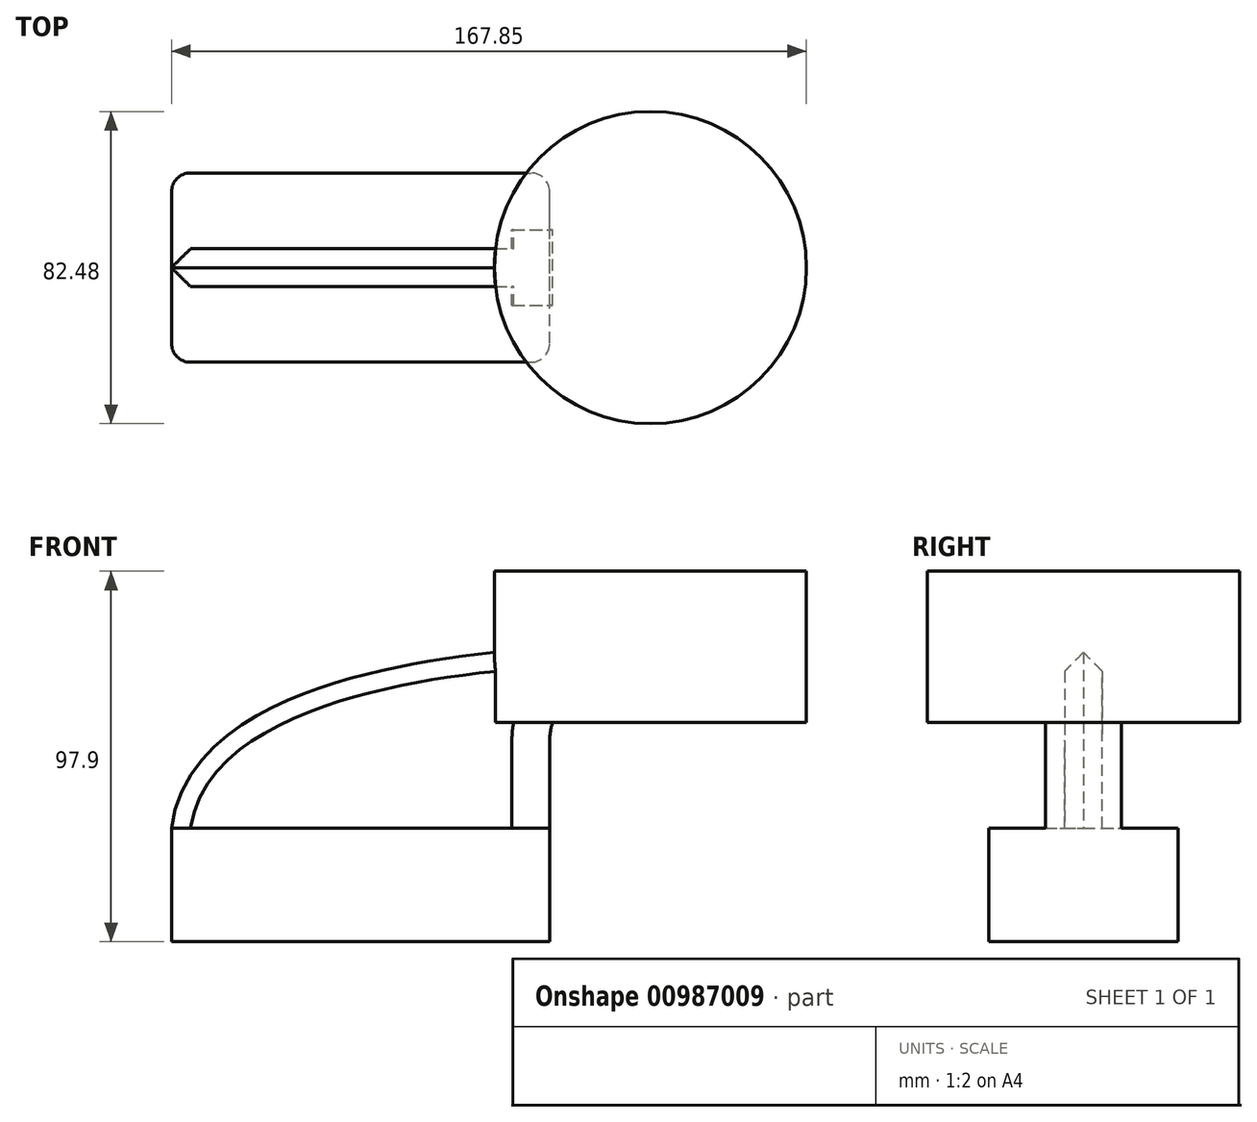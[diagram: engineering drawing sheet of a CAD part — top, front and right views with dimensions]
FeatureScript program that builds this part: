
annotation { "Feature Type Name" : "Feature", "Feature Type Description" : "" }
export const myFeature = defineFeature(function(context is Context, id is Id, definition is map)
    precondition{}
    {
        {
            var Q0;
            Q0=qCreatedBy(makeId("Front.planeOp"),FACE);
            var sketch = newSketch(context, id + "F0", { "sketchPlane" : qUnion([Q0])});
            skLineSegment(sketch, "E0.bottom", {"start": v(-50, 15) * mm, "end": v(50, 15) * mm});
            skLineSegment(sketch, "E0.top", {"start": v(-50, -15) * mm, "end": v(50, -15) * mm});
            skLineSegment(sketch, "E0.left", {"start": v(-50, 15) * mm, "end": v(-50, -15) * mm});
            skLineSegment(sketch, "E0.right", {"start": v(50, 15) * mm, "end": v(50, -15) * mm});
            skPoint(sketch, "E0.middle", {"position": v(0, 0) * mm});
            skLineSegment(sketch, "E1.bottom", {"start": v(76.6, 42.9) * mm, "end": v(117.85, 42.9) * mm});
            skLineSegment(sketch, "E1.top", {"start": v(76.6, 82.9) * mm, "end": v(117.85, 82.9) * mm});
            skLineSegment(sketch, "E1.left", {"start": v(76.6, 42.9) * mm, "end": v(76.6, 82.9) * mm});
            skLineSegment(sketch, "E1.right", {"start": v(117.85, 42.9) * mm, "end": v(117.85, 82.9) * mm});
            skPoint(sketch, "E1.middle", {"position": v(97.23, 62.9) * mm});
            skLineSegment(sketch, "E2", {"start": v(50, 15) * mm, "end": v(50, 38.22) * mm});
            skArc(sketch, "E3", {"start": v(50, 38.22) * mm, "mid": v(54.4, 48.82) * mm, "end": v(65, 53.22) * mm});
            skLineSegment(sketch, "E4", {"start": v(65, 53.22) * mm, "end": v(96.4, 53.22) * mm});
            skLineSegment(sketch, "E5.0", {"start": v(65, 63.22) * mm, "end": v(96.4, 63.22) * mm});
            skArc(sketch, "E5.1", {"start": v(40, 38.22) * mm, "mid": v(47.32, 55.9) * mm, "end": v(65, 63.22) * mm});
            skLineSegment(sketch, "E5.2", {"start": v(40, 15) * mm, "end": v(40, 38.22) * mm});
            skFitSpline(sketch, "E6", {"points": [v(-50, 15) * mm, v(65, 63.22) * mm], "startDerivative": vector(14.19, 117.72) * mm, "endDerivative": vector(125.03, 2.43) * mm});
            skSolve(sketch);
        }
        {
            var Q0;
            Q0=makeQuery(id+"F0.imprint","IMPRINT",FACE,{"disambiguationData":[TD([[makeQuery(id+"F0.imprint","IMPRINT",EDGE,{"derivedFrom":sQuery(id+"F0.wireOp",EDGE,"E0.top")}),1.0]])]});
            extrude(context, id + "F1", {"entities" : qUnion([Q0]), "endBound" : BoundingType.SYMMETRIC, "depth" : 50 * mm, "offsetDistance" : 25 * mm});
        }
        {
            var Q0;
            {var subQ1=sQuery(id+"F0.wireOp",EDGE,"E2");Q0=makeQuery(id+"F0.imprint","IMPRINT",FACE,{"disambiguationData":[TD([[makeQuery(id+"F0.imprint","IMPRINT",EDGE,{"derivedFrom":subQ1}),1.0]])]});}
            extrude(context, id + "F2", {"entities" : qUnion([Q0]), "operationType" : NewBodyOperationType.ADD, "endBound" : BoundingType.SYMMETRIC, "depth" : 20 * mm, "offsetDistance" : 25 * mm});
        }
        {
            var Q0;
            {var subQ3=sQuery(id+"F0.wireOp",EDGE,"E5.2");Q0=makeQuery(id+"F0.imprint","IMPRINT",FACE,{"disambiguationData":[TD([[makeQuery(id+"F0.imprint","IMPRINT",EDGE,{"derivedFrom":subQ3}),1.0]])]});}
            extrude(context, id + "F3", {"entities" : qUnion([Q0]), "operationType" : NewBodyOperationType.ADD, "endBound" : BoundingType.SYMMETRIC, "depth" : 10 * mm, "offsetDistance" : 25 * mm});
        }
        {
            var Q0;
            {var subQ3=sQuery(id+"F0.wireOp",EDGE,"E1.bottom");Q0=makeQuery(id+"F0.imprint","IMPRINT",FACE,{"disambiguationData":[TD([[makeQuery(id+"F0.imprint","IMPRINT",EDGE,{"derivedFrom":subQ3}),1.0]])]});}
            var Q1;
            Q1=sQuery(id+"F0.wireOp",EDGE,"E1.left");
            revolve(context, id + "F4", {"operationType" : NewBodyOperationType.ADD, "surfaceOperationType" : NewSurfaceOperationType.NEW, "entities" : qUnion([Q0]), "axis" : qUnion([Q1]), "revolveType" : RevolveType.FULL});
        }
        {
            var Q0;
            Q0=makeQuery(id+"F1.opExtrude","CAP_EDGE",EDGE,{"disambiguationData":[OSD([sQuery(id+"F0.wireOp",EDGE,"E0.right")])],"isStart":false});
            var Q1;
            Q1=makeQuery(id+"F1.opExtrude","CAP_EDGE",EDGE,{"disambiguationData":[OSD([sQuery(id+"F0.wireOp",EDGE,"E0.left")])],"isStart":false});
            var Q2;
            Q2=makeQuery(id+"F1.opExtrude","CAP_EDGE",EDGE,{"disambiguationData":[OSD([sQuery(id+"F0.wireOp",EDGE,"E0.right")])],"isStart":true});
            var Q3;
            Q3=makeQuery(id+"F1.opExtrude","CAP_EDGE",EDGE,{"disambiguationData":[OSD([sQuery(id+"F0.wireOp",EDGE,"E0.left")])],"isStart":true});
            fillet(context, id + "F5", {"entities" : qUnion([Q0, Q1, Q2, Q3]), "radius" : 5 * mm, "tangentPropagation" : true, "allowEdgeOverflow" : false});
        }
        {
            var Q0;
            Q0=makeQuery(id+"F3.opExtrude","CAP_EDGE",EDGE,{"disambiguationData":[OSD([sQuery(id+"F0.wireOp",EDGE,"E6")])],"isStart":false});
            var Q1;
            Q1=makeQuery(id+"F3.opExtrude","CAP_EDGE",EDGE,{"disambiguationData":[OSD([sQuery(id+"F0.wireOp",EDGE,"E6")])],"isStart":true});
            chamfer(context, id + "F6", {"entities" : qUnion([Q0, Q1]), "width" : 5 * mm, "tangentPropagation" : true});
        }
    });
